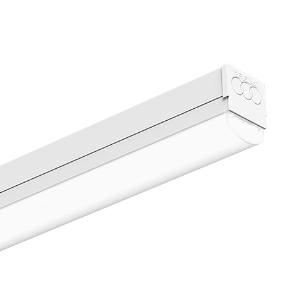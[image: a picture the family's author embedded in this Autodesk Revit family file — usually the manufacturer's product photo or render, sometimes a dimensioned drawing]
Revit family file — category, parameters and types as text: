
# Revit family: 3f_filippi_-_3f_zeta_d_3f_filippi_-_10871_-_3f_zeta_d_1x18_led_l1194
name_source: partatom
category: Lighting Fixtures
units: mm (PartAtom-declared; Revit-internal decimal feet)

## family parameters
Cut with Voids When Loaded = No
Host = Face
Light Source = No
Part Type = Normal
Room Calculation Point = No
Round Connector Dimension = Use Diameter
Shared = No

## types (1)
- 3F Filippi - 3F Zeta D (1 x LED, 2419 lm, 20 W, 4000 K)
    Apparent Load = 20 VA
    Approval mark = CE
    CIE Flux Codes = 42 71 90 91 100
    Color Rendering = 80
    Color Temperature = 4000 K
    Control Gear = Electronic ballast
    Default Elevation = 1800 mm
    Description = ILLUMINOTECHNICAL
Luminous efficiency 100% (DLOR 91%, ULOR 9%).
Initial luminous flux of the luminaire 2419 lm.
Diffused symmetric distribution.
Installation Interdistance Transv.D = 1.31 x hu - Long.D = 1.25 x hu.
Tabular UGR (CIE 117 - 4H-8H; S=0.25H; 70/50/20): RUG 23.7 - 22.
Beam angle: 130° - 112°.
Luminous efficacy 121 lm/W.
Lifetime (L93/B10): 30000 h. (tq+25°C)
Lifetime (L90/B10): 50000 h. (tq+25°C)
Lifetime (L85/B10): 80000 h. (tq+25°C)
Lifetime (L80/B10): 100000 h. (tq+25°C)
Sudden decreased luminous flux after 50000 hours: 0% (C0).
Photobiological safety in compliance with IEC/TR 62778: RG0 risk exempt, (IEC 62471).
In compliance with IEC/EN 62722-2-1 - IEC/EN 62717 standards.

SOURCE
Linear LED module 18W/840.
Energy efficiency class (UE 2019/2020 - UE 2019/2015): D.
CIE 13.3 Colour rendering index: CRI >80 (R9 <50%).
IES TM-30 Fidelity Index: Rf = 84 Rg = 95.
CCT nominal colour temperature 4000 K.
Colour initial tolerance (MacAdam): SDCM 3.

MECHANICAL
Housing in hot-galvanised steel, painted in white polyester, obtained through rolling process.
Light unit in hot-galvanised steel, painted in white polyester base with fixing springs and retractable safety hooks in stainless steel.
Curved screen in self-extinguishing polycarbonate, UV stabilised, opal, with smooth outer surface.
End caps in white polycarbonate.
Pair of stainless steel sliding brackets with sliding block screws.
Luminaire with limited surface temperature. - D - (EN 60598-2-24)
Dimensions: 1194x62 mm, height 81 mm. Weight 2.81 kg.
IP40 protection degree.
Mechanical strength to impacts IK06 (1 joule).
Glow-wire test resistance 850°C.

ELECTRICAL
Halogen Free electronic wiring 230V-50/60Hz, power factor 0.90, THD <25%, constant output current, SELV, class I, 1 driver.
Power of the luminaire 20 W.
ENEC - CE.
SAFE FLICKER: PstLM=<1 and SVM=<0.4 (IEC TR 61547-1 and IEC TR 63158), to ensure a more comfortable and safe light.
Luminaire compliant with EN 60598-2-22 for power supply from a centralised emergency system CPSS (Central Power Supply System), not incorporated in the luminaire - high risk areas excluded. The default power and flux are 100% in AC and 100% in DC.
Ambient temperature from 0°C to +25°C.
Temperature class T6 max 85°C.
Relative humidity UR: <85%.

INSTALLATION
Ceiling / Suspended / Wall.
All accessories dedicated to this product are available on the Catalog and on our website www.3F-Filippi.com.

APPLICATIONS
Suitable product for food production plants (HACCP), IFS (Food Version 6), BRC (GSFS Food Version 7).
In commercial environments, exhibition areas, shops and stores.

WARNING
Luminaire designed for disposal/recycling at end-of-life.
Replaceable (LED only) light source by a professional. Replaceable control gear by a professional.
    Height = 81 mm
    Lamp = 1 x LED
    Lamp Light Flux = 2419 lm
    Lamp Power = 20 W
    Lamp count = 1
    Length = 1194 mm
    Lifetime = 50000 h
    Luminous efficacy = 121 lm/W
    Manufacturer = 3F Filippi
    ModVariant = No
    Model = 3F Filippi - 10871 - 3F Zeta D 1x18 LED L1194
    Mounting Place = Ceiling
    Mounting Type = Pendant
    Number of Poles = 1
    OnlyDefault = Yes
    Power Factor = 1
    Product Name = 3F Filippi - 3F Zeta D
    Product group = pendant luminaire
    ProductGroupID = 9
    Protection Class = Protection class I
    Protection Degree = IP 40
    RLX_Detail_Level = 1
    RLX_Emergency_Light_Flux = 0 lm
    RLX_Emergency_Type = 0
    RLX_Emergency_Type_DB = No
    RlxData = <blob elided: 33361 chars, md5=2028fa82>
    Socket = socket
    Standby Power = 0 W
    System Light Flux = 2419 lm
    System Power = 20 W
    Type Comments = Product without accessories
    Type Image = 3ffilippi_3f_zeta_d.jpg
    URL = http://relux.com
    VarID = ---
    Voltage = 0 V
    Weight = 0.00 kg
    Width = 62 mm

## geometry (parser evidence)
native form markers: Blend x4, Sweep x10
no freeform markers — native parametric forms only
